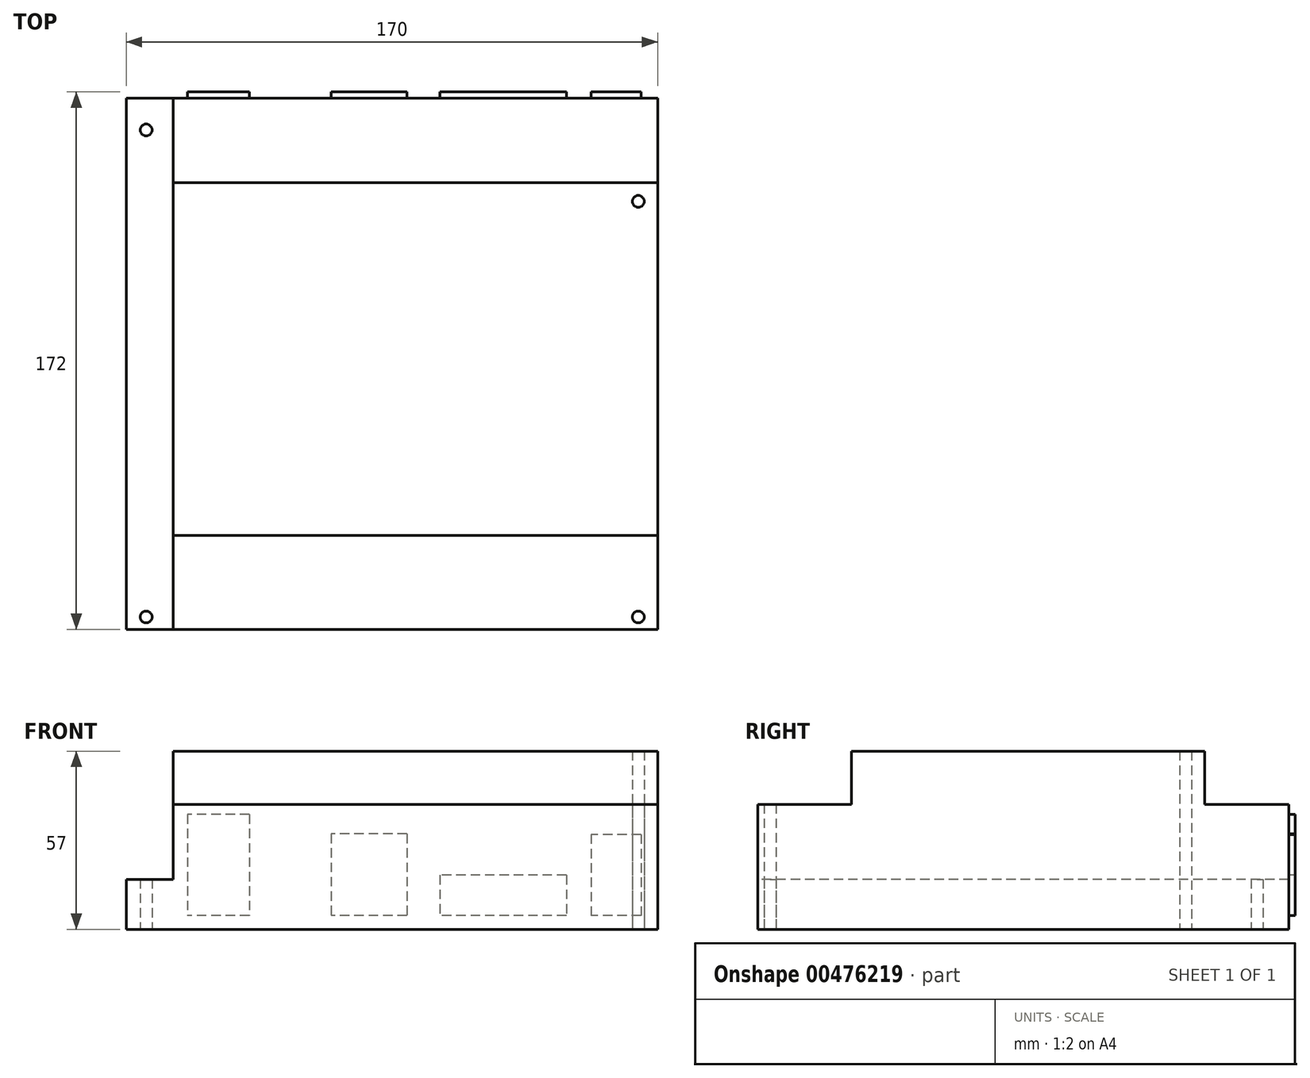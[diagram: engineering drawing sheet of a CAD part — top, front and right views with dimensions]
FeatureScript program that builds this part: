
annotation { "Feature Type Name" : "Feature", "Feature Type Description" : "" }
export const myFeature = defineFeature(function(context is Context, id is Id, definition is map)
    precondition{}
    {
        {
            var Q0;
            Q0=qCreatedBy(makeId("Top.planeOp"),FACE);
            var sketch = newSketch(context, id + "F0", { "sketchPlane" : qUnion([Q0])});
            skLineSegment(sketch, "E0.bottom", {"start": v(-85, 85) * mm, "end": v(85, 85) * mm});
            skLineSegment(sketch, "E0.top", {"start": v(-85, -85) * mm, "end": v(85, -85) * mm});
            skLineSegment(sketch, "E0.left", {"start": v(-85, 85) * mm, "end": v(-85, -85) * mm});
            skLineSegment(sketch, "E0.right", {"start": v(85, 85) * mm, "end": v(85, -85) * mm});
            skSolve(sketch);
        }
        {
            var Q0;
            Q0=makeQuery(id+"F0.imprint","IMPRINT",FACE,{"disambiguationData":[TD([[makeQuery(id+"F0.imprint","IMPRINT",EDGE,{"derivedFrom":sQuery(id+"F0.wireOp",EDGE,"E0.bottom")}),-1.0]])]});
            extrude(context, id + "F1", {"entities" : qUnion([Q0]), "depth" : 40 * mm});
        }
        {
            var Q0;
            Q0=makeQuery(id+"F1.opExtrude","CAP_FACE",FACE,{"disambiguationData":[OSD([sQuery(id+"F0.wireOp",EDGE,"E0.bottom"),sQuery(id+"F0.wireOp",EDGE,"E0.top"),sQuery(id+"F0.wireOp",EDGE,"E0.left"),sQuery(id+"F0.wireOp",EDGE,"E0.right")])],"isStart":false});
            var sketch = newSketch(context, id + "F2", { "sketchPlane" : qUnion([Q0])});
            skLineSegment(sketch, "E1", {"start": v(-70, 85) * mm, "end": v(-70, -85) * mm});
            skLineSegment(sketch, "E2", {"start": v(-70, 58) * mm, "end": v(85, 58) * mm});
            skLineSegment(sketch, "E3", {"start": v(85, -55) * mm, "end": v(-70, -55) * mm});
            skSolve(sketch);
        }
        {
            var Q0;
            {var subQ0=sQuery(id+"F2.wireOp",EDGE,"E2");Q0=makeQuery(id+"F2.imprint","IMPRINT",FACE,{"disambiguationData":[TD([[makeQuery(id+"F2.imprint","IMPRINT",EDGE,{"derivedFrom":subQ0}),-1.0]])]});}
            extrude(context, id + "F3", {"entities" : qUnion([Q0]), "operationType" : NewBodyOperationType.ADD, "depth" : 17 * mm});
        }
        {
            var Q0;
            {var subQ5=makeQuery(id+"F1.opExtrude","CAP_EDGE",EDGE,{"disambiguationData":[OSD([sQuery(id+"F0.wireOp",EDGE,"E0.left")])],"isStart":false});Q0=makeQuery(id+"F2.imprint","IMPRINT",FACE,{"disambiguationData":[TD([[makeQuery(id+"F2.imprint","IMPRINT",EDGE,{"derivedFrom":subQ5}),1.0]])]});}
            extrude(context, id + "F4", {"entities" : qUnion([Q0]), "operationType" : NewBodyOperationType.REMOVE, "oppositeDirection" : true, "depth" : (40 - 16) * mm});
        }
        {
            var Q0;
            Q0=makeQuery(id+"F1.opExtrude","CAP_FACE",FACE,{"disambiguationData":[OSD([sQuery(id+"F0.wireOp",EDGE,"E0.bottom"),sQuery(id+"F0.wireOp",EDGE,"E0.top"),sQuery(id+"F0.wireOp",EDGE,"E0.left"),sQuery(id+"F0.wireOp",EDGE,"E0.right")])],"isStart":true});
            var sketch = newSketch(context, id + "F5", { "sketchPlane" : qUnion([Q0])});
            skPoint(sketch, "E4", {"position": v(-78.65, -74.84) * mm});
            skPoint(sketch, "E5", {"position": v(-78.65, 81.04) * mm});
            skPoint(sketch, "E6", {"position": v(78.83, 81.04) * mm});
            skPoint(sketch, "E7", {"position": v(78.83, -51.98) * mm});
            skSolve(sketch);
        }
        {
            var Q0;
            Q0=sQuery(id+"F5.wireOp",VERTEX,"E4");
            var Q1;
            Q1=sQuery(id+"F5.wireOp",VERTEX,"E7");
            var Q2;
            Q2=sQuery(id+"F5.wireOp",VERTEX,"E6");
            var Q3;
            Q3=sQuery(id+"F5.wireOp",VERTEX,"E5");
            var Q4;
            Q4=makeQuery(id+"F1.opExtrude","SWEPT_BODY",BODY,{"disambiguationData":[OSD([sQuery(id+"F0.wireOp",EDGE,"E0.bottom"),sQuery(id+"F0.wireOp",EDGE,"E0.top"),sQuery(id+"F0.wireOp",EDGE,"E0.left"),sQuery(id+"F0.wireOp",EDGE,"E0.right")])]});
            hole(context, id + "F6", {"style" : HoleStyle.SIMPLE, "endStyle" : HoleEndStyle.THROUGH, "standardTappedOrClearance" : lookupTablePath({ "standard" : "ANSI", "fit" : "Normal (ASME)", "size" : "#6", "type" : "Clearance" }), "standardBlindInLast" : lookupTablePath({ "fit" : "Free", "standard" : "ANSI", "size" : "#6", "type" : "Clearance" }), "holeDiameter" : 3.8 * mm, "isTappedThrough" : true, "tappedDepth" : 3.8 * mm, "tapClearance" : 0, "locations" : qUnion([Q0, Q1, Q2, Q3]), "scope" : qUnion([Q4])});
        }
        {
            var Q0;
            Q0=makeQuery(id+"F1.opExtrude","SWEPT_FACE",FACE,{"disambiguationData":[OSD([sQuery(id+"F0.wireOp",EDGE,"E0.bottom")])]});
            var sketch = newSketch(context, id + "F7", { "sketchPlane" : qUnion([Q0])});
            skLineSegment(sketch, "E8.bottom", {"start": v(-79.72, 30.33) * mm, "end": v(-63.71, 30.33) * mm});
            skLineSegment(sketch, "E8.top", {"start": v(-79.72, 4.45) * mm, "end": v(-63.71, 4.45) * mm});
            skLineSegment(sketch, "E8.left", {"start": v(-79.72, 30.33) * mm, "end": v(-79.72, 4.45) * mm});
            skLineSegment(sketch, "E8.right", {"start": v(-63.71, 30.33) * mm, "end": v(-63.71, 4.45) * mm});
            skLineSegment(sketch, "E9.bottom", {"start": v(-55.8, 17.3) * mm, "end": v(-15.39, 17.3) * mm});
            skLineSegment(sketch, "E9.top", {"start": v(-55.8, 4.45) * mm, "end": v(-15.39, 4.45) * mm});
            skLineSegment(sketch, "E9.left", {"start": v(-55.8, 17.3) * mm, "end": v(-55.8, 4.45) * mm});
            skLineSegment(sketch, "E9.right", {"start": v(-15.39, 17.3) * mm, "end": v(-15.39, 4.45) * mm});
            skLineSegment(sketch, "E10.bottom", {"start": v(-4.76, 30.54) * mm, "end": v(19.47, 30.54) * mm});
            skLineSegment(sketch, "E10.top", {"start": v(-4.76, 4.45) * mm, "end": v(19.47, 4.45) * mm});
            skLineSegment(sketch, "E10.left", {"start": v(-4.76, 30.54) * mm, "end": v(-4.76, 4.45) * mm});
            skLineSegment(sketch, "E10.right", {"start": v(19.47, 30.54) * mm, "end": v(19.47, 4.45) * mm});
            skLineSegment(sketch, "E11.bottom", {"start": v(45.62, 36.76) * mm, "end": v(65.47, 36.76) * mm});
            skLineSegment(sketch, "E11.top", {"start": v(45.62, 4.45) * mm, "end": v(65.47, 4.45) * mm});
            skLineSegment(sketch, "E11.left", {"start": v(45.62, 36.76) * mm, "end": v(45.62, 4.45) * mm});
            skLineSegment(sketch, "E11.right", {"start": v(65.47, 36.76) * mm, "end": v(65.47, 4.45) * mm});
            skLineSegment(sketch, "E12", {"start": v(-63.71, 4.45) * mm, "end": v(-55.8, 4.45) * mm, "construction": true});
            skLineSegment(sketch, "E13", {"start": v(-15.39, 4.45) * mm, "end": v(-4.76, 4.45) * mm, "construction": true});
            skLineSegment(sketch, "E14", {"start": v(19.47, 4.45) * mm, "end": v(45.62, 4.45) * mm, "construction": true});
            skSolve(sketch);
        }
        {
            var Q0;
            Q0=makeQuery(id+"F7.imprint","IMPRINT",FACE,{"disambiguationData":[TD([[makeQuery(id+"F7.imprint","IMPRINT",EDGE,{"derivedFrom":sQuery(id+"F7.wireOp",EDGE,"E8.bottom")}),-1.0]])]});
            var Q1;
            Q1=makeQuery(id+"F7.imprint","IMPRINT",FACE,{"disambiguationData":[TD([[makeQuery(id+"F7.imprint","IMPRINT",EDGE,{"derivedFrom":sQuery(id+"F7.wireOp",EDGE,"E9.bottom")}),-1.0]])]});
            var Q2;
            Q2=makeQuery(id+"F7.imprint","IMPRINT",FACE,{"disambiguationData":[TD([[makeQuery(id+"F7.imprint","IMPRINT",EDGE,{"derivedFrom":sQuery(id+"F7.wireOp",EDGE,"E10.bottom")}),-1.0]])]});
            var Q3;
            Q3=makeQuery(id+"F7.imprint","IMPRINT",FACE,{"disambiguationData":[TD([[makeQuery(id+"F7.imprint","IMPRINT",EDGE,{"derivedFrom":sQuery(id+"F7.wireOp",EDGE,"E11.bottom")}),-1.0]])]});
            extrude(context, id + "F8", {"entities" : qUnion([Q0, Q1, Q2, Q3]), "operationType" : NewBodyOperationType.ADD, "depth" : 2 * mm});
        }
    });
